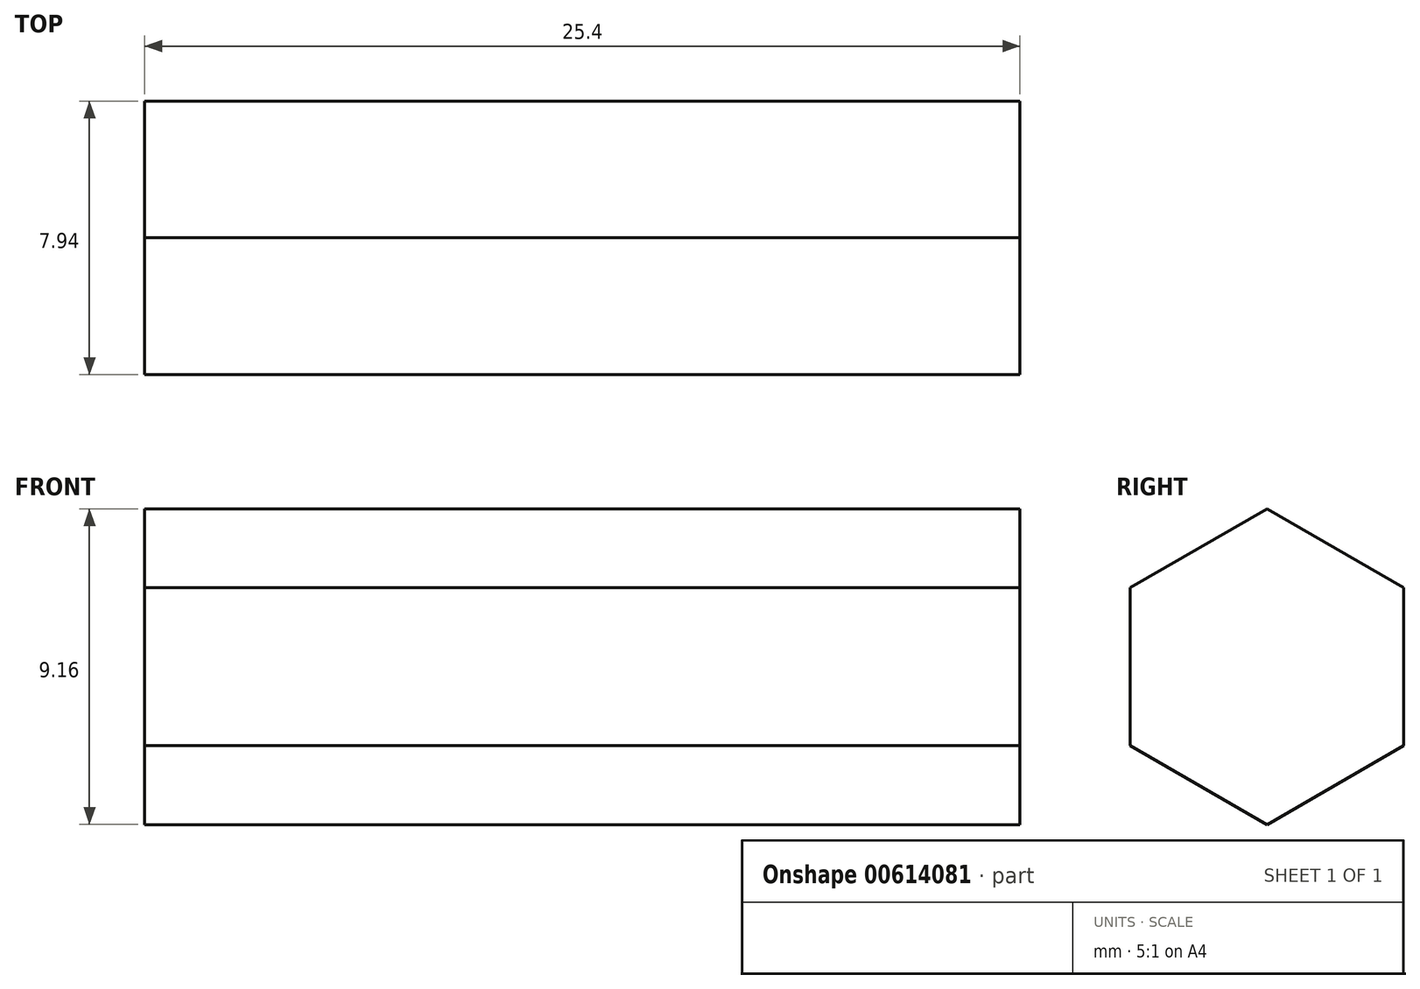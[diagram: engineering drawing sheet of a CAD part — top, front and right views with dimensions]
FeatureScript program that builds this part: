
annotation { "Feature Type Name" : "Feature", "Feature Type Description" : "" }
export const myFeature = defineFeature(function(context is Context, id is Id, definition is map)
    precondition{}
    {
        {
            var Q0;
            Q0=qCreatedBy(makeId("Right.planeOp"),FACE);
            var sketch = newSketch(context, id + "F0", { "sketchPlane" : qUnion([Q0])});
            skCircle(sketch, "E0.cCircle", {"center": v(0, 0) * mm, "radius": 3.97 * mm, "construction": true});
            skLineSegment(sketch, "E0.0", {"start": v(3.97, -2.3) * mm, "end": v(0, -4.58) * mm});
            skLineSegment(sketch, "E0.1", {"start": v(0, -4.58) * mm, "end": v(-3.97, -2.3) * mm});
            skLineSegment(sketch, "E0.2", {"start": v(-3.97, -2.3) * mm, "end": v(-3.97, 2.3) * mm});
            skLineSegment(sketch, "E0.3", {"start": v(-3.97, 2.3) * mm, "end": v(0, 4.58) * mm});
            skLineSegment(sketch, "E0.4", {"start": v(0, 4.58) * mm, "end": v(3.97, 2.3) * mm});
            skLineSegment(sketch, "E0.5", {"start": v(3.97, 2.3) * mm, "end": v(3.97, -2.3) * mm});
            skPoint(sketch, "E0.0.midPoint", {"position": v(1.98, -3.44) * mm});
            skSolve(sketch);
        }
        {
            var Q0;
            Q0=makeQuery(id+"F0.imprint","IMPRINT",FACE,{"disambiguationData":[TD([[makeQuery(id+"F0.imprint","IMPRINT",EDGE,{"derivedFrom":sQuery(id+"F0.wireOp",EDGE,"E0.0")}),-1.0]])]});
            extrude(context, id + "F1", {"entities" : qUnion([Q0]), "depth" : 25.4 * mm, "offsetDistance" : 25.4 * mm});
        }
    });
